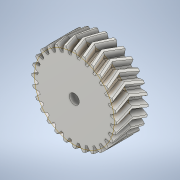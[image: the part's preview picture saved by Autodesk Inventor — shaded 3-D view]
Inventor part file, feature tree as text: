
AUTODESK INVENTOR PART (.ipt)
format: ipt  version: 2020 (Build 240168000, 168)  size: 728,576 bytes
history: native  units: mm (DEFAULTED — no unit token found)
features: other x4, extrude x3, plane x3, sketch x3, mirror x1
ambient origin geometry x8: Origin, YZ Plane, XZ Plane, XY Plane, X Axis, Y Axis, Z Axis, Center Point
bodies: Solid1 (feature_tree)
feature tree (14):
  extrude  "Extrusion1"  Depth=5.0mm TaperAngle=0.0deg
  plane  "Work Plane2"
  plane  "Work Plane8"
  plane  "Work Plane9"
  other  "Spur Gear"
  mirror  "Mirror1"
  extrude  "Extrusion2"  Depth=10.0mm TaperAngle=0.0deg
  sketch  "Sketch1"  dims[d0=27.133641mm d1=5.0mm d2=0.0mm]
  sketch  "Sketch2"  dims[d3=25.454545mm d4=10.0mm d5=0.0mm]
  other  "Srf1"
  other  "Srf2"
  sketch  "Sketch3"  dims[d16=25.0mm d17=0.0mm d34=1.121997mm d39=0.0mm d41=0.0mm d43=25.0mm d46=25.0mm d47=0.0mm d48=0.0mm d49=3.2mm d50=10.0mm d51=0.0mm]
  other  "Pitch Diameter"
  extrude  "ExtrusionSrf2"  Depth=10.0mm TaperAngle=0.0deg
